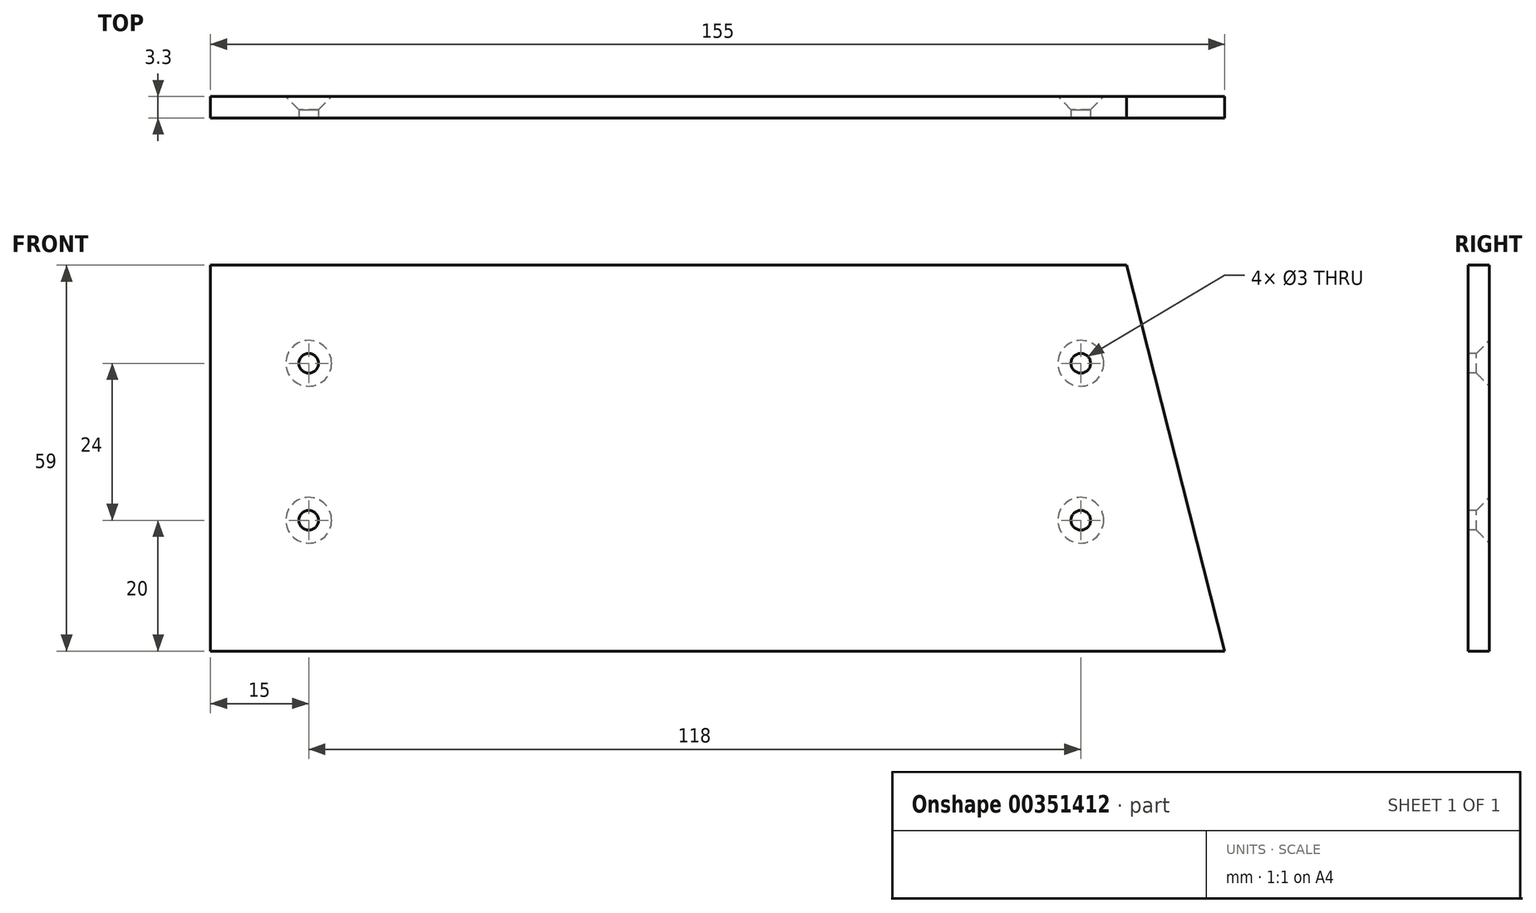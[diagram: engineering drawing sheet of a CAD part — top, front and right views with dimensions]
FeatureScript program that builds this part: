
annotation { "Feature Type Name" : "Feature", "Feature Type Description" : "" }
export const myFeature = defineFeature(function(context is Context, id is Id, definition is map)
    precondition{}
    {
        {
            var Q0;
            Q0=qCreatedBy(makeId("Front.planeOp"),FACE);
            var sketch = newSketch(context, id + "F0", { "sketchPlane" : qUnion([Q0])});
            skLineSegment(sketch, "E0.bottom", {"start": v(70, 29.5) * mm, "end": v(-70, 29.5) * mm});
            skLineSegment(sketch, "E0.top", {"start": v(70, -29.5) * mm, "end": v(-70, -29.5) * mm});
            skLineSegment(sketch, "E0.left", {"start": v(70, 29.5) * mm, "end": v(70, -29.5) * mm});
            skLineSegment(sketch, "E0.right", {"start": v(-70, 29.5) * mm, "end": v(-70, -29.5) * mm});
            skPoint(sketch, "E0.middle", {"position": v(0, 0) * mm});
            skLineSegment(sketch, "E1", {"start": v(70, 29.5) * mm, "end": v(85, -29.5) * mm});
            skLineSegment(sketch, "E2", {"start": v(85, -29.5) * mm, "end": v(70, -29.5) * mm});
            skSolve(sketch);
        }
        {
            var Q0;
            Q0=qSketchRegion(id+"F0",true);
            extrude(context, id + "F1", {"entities" : qUnion([Q0]), "depth" : 3.3 * mm});
        }
        {
            var Q0;
            Q0=makeQuery(id+"F1.opExtrude","CAP_FACE",FACE,{"disambiguationData":[OSD([sQuery(id+"F0.wireOp",EDGE,"E0.bottom"),sQuery(id+"F0.wireOp",EDGE,"E0.top"),sQuery(id+"F0.wireOp",EDGE,"E0.right"),sQuery(id+"F0.wireOp",EDGE,"E1"),sQuery(id+"F0.wireOp",EDGE,"E2")])],"isStart":false});
            var sketch = newSketch(context, id + "F2", { "sketchPlane" : qUnion([Q0])});
            skCircle(sketch, "E3", {"center": v(-55, 14.5) * mm, "radius": 1.5 * mm});
            skCircle(sketch, "E4", {"center": v(63, 14.5) * mm, "radius": 1.5 * mm});
            skCircle(sketch, "E5", {"center": v(63, -9.5) * mm, "radius": 1.5 * mm});
            skCircle(sketch, "E6", {"center": v(-55, -9.5) * mm, "radius": 1.5 * mm});
            skLineSegment(sketch, "E7", {"start": v(70, 29.5) * mm, "end": v(70, -29.5) * mm, "construction": true});
            skSolve(sketch);
        }
        {
            var Q0;
            Q0=qSketchRegion(id+"F2",true);
            extrude(context, id + "F3", {"entities" : qUnion([Q0]), "operationType" : NewBodyOperationType.REMOVE, "oppositeDirection" : true, "depth" : 25 * mm});
        }
        {
            var Q0;
            Q0=makeQuery(id+"F3.boolean.opBoolean","INTERSECT",EDGE,{"derivedFrom":[makeQuery(id+"F1.opExtrude","CAP_FACE",FACE,{"disambiguationData":[OSD([sQuery(id+"F0.wireOp",EDGE,"E0.bottom"),sQuery(id+"F0.wireOp",EDGE,"E0.top"),sQuery(id+"F0.wireOp",EDGE,"E0.right"),sQuery(id+"F0.wireOp",EDGE,"E1"),sQuery(id+"F0.wireOp",EDGE,"E2")])],"isStart":true}),makeQuery(id+"F3.opExtrude","SWEPT_FACE",FACE,{"disambiguationData":[OSD([sQuery(id+"F2.wireOp",EDGE,"E6")])]})]});
            var Q1;
            Q1=makeQuery(id+"F3.boolean.opBoolean","INTERSECT",EDGE,{"derivedFrom":[makeQuery(id+"F1.opExtrude","CAP_FACE",FACE,{"disambiguationData":[OSD([sQuery(id+"F0.wireOp",EDGE,"E0.bottom"),sQuery(id+"F0.wireOp",EDGE,"E0.top"),sQuery(id+"F0.wireOp",EDGE,"E0.right"),sQuery(id+"F0.wireOp",EDGE,"E1"),sQuery(id+"F0.wireOp",EDGE,"E2")])],"isStart":true}),makeQuery(id+"F3.opExtrude","SWEPT_FACE",FACE,{"disambiguationData":[OSD([sQuery(id+"F2.wireOp",EDGE,"E3")])]})]});
            var Q2;
            Q2=makeQuery(id+"F3.boolean.opBoolean","INTERSECT",EDGE,{"derivedFrom":[makeQuery(id+"F1.opExtrude","CAP_FACE",FACE,{"disambiguationData":[OSD([sQuery(id+"F0.wireOp",EDGE,"E0.bottom"),sQuery(id+"F0.wireOp",EDGE,"E0.top"),sQuery(id+"F0.wireOp",EDGE,"E0.right"),sQuery(id+"F0.wireOp",EDGE,"E1"),sQuery(id+"F0.wireOp",EDGE,"E2")])],"isStart":true}),makeQuery(id+"F3.opExtrude","SWEPT_FACE",FACE,{"disambiguationData":[OSD([sQuery(id+"F2.wireOp",EDGE,"E5")])]})]});
            var Q3;
            Q3=makeQuery(id+"F3.boolean.opBoolean","INTERSECT",EDGE,{"derivedFrom":[makeQuery(id+"F1.opExtrude","CAP_FACE",FACE,{"disambiguationData":[OSD([sQuery(id+"F0.wireOp",EDGE,"E0.bottom"),sQuery(id+"F0.wireOp",EDGE,"E0.top"),sQuery(id+"F0.wireOp",EDGE,"E0.right"),sQuery(id+"F0.wireOp",EDGE,"E1"),sQuery(id+"F0.wireOp",EDGE,"E2")])],"isStart":true}),makeQuery(id+"F3.opExtrude","SWEPT_FACE",FACE,{"disambiguationData":[OSD([sQuery(id+"F2.wireOp",EDGE,"E4")])]})]});
            chamfer(context, id + "F4", {"entities" : qUnion([Q0, Q1, Q2, Q3]), "width" : 2 * mm, "tangentPropagation" : true});
        }
    });
